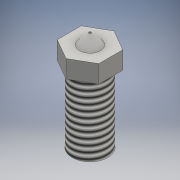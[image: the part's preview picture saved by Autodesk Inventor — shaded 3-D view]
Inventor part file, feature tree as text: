
AUTODESK INVENTOR PART (.ipt)
format: ipt  version: 2016 SP1 (Build 200210100, 210)  size: 139,264 bytes
history: native  units: mm
features: sketch x6, extrude x4, plane x1, revolve x1, thread x1
ambient origin geometry x8: Origin, YZ Plane, XZ Plane, XY Plane, X Axis, Y Axis, Z Axis, Center Point
bodies: Solid1 (feature_tree)
feature tree (13):
  extrude  "Extrusion1"  Depth=12.0mm TaperAngle=0.0deg
  extrude  "Extrusion2"  Depth=3.0mm TaperAngle=0.0deg
  sketch  "Sketch3"  dims[d6=2.0mm d7=1.75mm]
  plane  "Work Plane1"
  revolve  "Revolution1"  [1 undecoded]
  extrude  "Extrusion3"  Depth=2.0mm
  extrude  "Extrusion4"  Depth=15.0mm
  thread  "Thread1"  [1 undecoded]
  sketch  "Sketch1"  dims[d0=6.0mm d1=12.0mm d2=0.0mm]
  sketch  "Sketch2"  dims[d3=7.0mm d4=3.0mm d5=0.0mm]
  sketch  "Sketch4"  dims[d8=1.75mm d9=2.0mm]
  sketch  "Sketch5"  dims[d10=90.0deg d11=1.75mm d12=15.0mm d13=0.0mm]
  sketch  "Sketch6"  dims[d14=0.4mm d15=3.0mm d16=0.0mm d17=10.0mm d18=0.0mm]
note: 2 required parameter values undecoded (feature->parameter linkage not recoverable at this tier; creation-order binding heuristic only, values carry confidence <= 0.55)